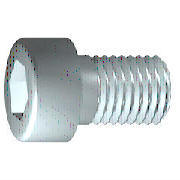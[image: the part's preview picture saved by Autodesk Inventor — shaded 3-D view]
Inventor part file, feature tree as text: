
AUTODESK INVENTOR PART (.ipt)
format: ipt  version: 2024.3 (Build 283343000, 343)  size: 194,560 bytes
history: native  units: mm (DEFAULTED — no unit token found)
features: extrude x1, plane x1, fillet x1
ambient origin geometry x7: Origin, YZ Plane, XY Plane, X Axis, Y Axis, Z Axis, Center Point
bodies: Solid1 (feature_tree), Body (feature_tree)
feature tree (3):
  extrude  "Slot"  Depth=16.875mm
  plane  "Work Plane1"
  fillet  "Fillet2"  Radius=0.766912mm
